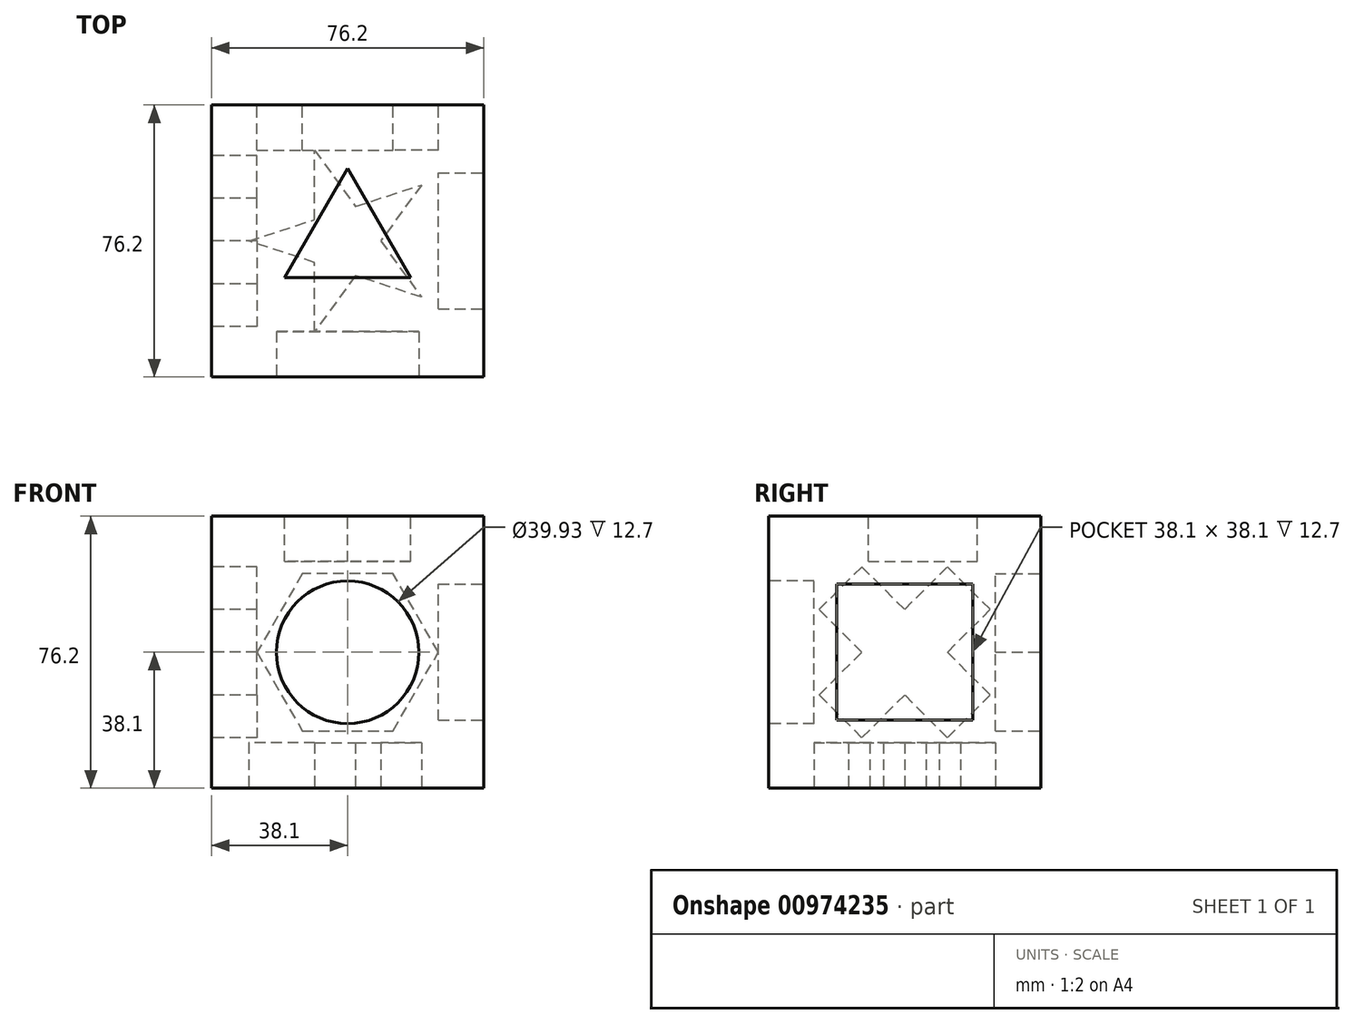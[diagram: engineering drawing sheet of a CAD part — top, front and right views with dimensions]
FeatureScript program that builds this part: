
annotation { "Feature Type Name" : "Feature", "Feature Type Description" : "" }
export const myFeature = defineFeature(function(context is Context, id is Id, definition is map)
    precondition{}
    {
        {
            var Q0;
            Q0=qCreatedBy(makeId("Front.planeOp"),FACE);
            var sketch = newSketch(context, id + "F0", { "sketchPlane" : qUnion([Q0])});
            skLineSegment(sketch, "E0.bottom", {"start": v(-38.1, -38.1) * mm, "end": v(38.1, -38.1) * mm});
            skLineSegment(sketch, "E0.top", {"start": v(-38.1, 38.1) * mm, "end": v(38.1, 38.1) * mm});
            skLineSegment(sketch, "E0.left", {"start": v(-38.1, -38.1) * mm, "end": v(-38.1, 38.1) * mm});
            skLineSegment(sketch, "E0.right", {"start": v(38.1, -38.1) * mm, "end": v(38.1, 38.1) * mm});
            skLineSegment(sketch, "E1", {"start": v(-38.1, 38.1) * mm, "end": v(38.1, -38.1) * mm, "construction": true});
            skSolve(sketch);
        }
        {
            var Q0;
            Q0=makeQuery(id+"F0.imprint","IMPRINT",FACE,{"disambiguationData":[TD([[makeQuery(id+"F0.imprint","IMPRINT",EDGE,{"derivedFrom":sQuery(id+"F0.wireOp",EDGE,"E0.bottom")}),1.0]])]});
            extrude(context, id + "F1", {"entities" : qUnion([Q0]), "depth" : 76.2 * mm, "offsetDistance" : 25.4 * mm});
        }
        {
            var Q0;
            Q0=makeQuery(id+"F1.opExtrude","CAP_FACE",FACE,{"disambiguationData":[OSD([sQuery(id+"F0.wireOp",EDGE,"E0.bottom"),sQuery(id+"F0.wireOp",EDGE,"E0.top"),sQuery(id+"F0.wireOp",EDGE,"E0.left"),sQuery(id+"F0.wireOp",EDGE,"E0.right")])],"isStart":false});
            var sketch = newSketch(context, id + "F2", { "sketchPlane" : qUnion([Q0])});
            skCircle(sketch, "E2", {"center": v(0, 0) * mm, "radius": 19.97 * mm});
            skSolve(sketch);
        }
        {
            var Q0;
            Q0 = qSketchRegion(id + "F2", true);
            var Q1;
            Q1=makeQuery(id+"F2.imprint","IMPRINT",FACE,{"disambiguationData":[TD([[makeQuery(id+"F2.imprint","IMPRINT",EDGE,{"derivedFrom":sQuery(id+"F2.wireOp",EDGE,"E2")}),1.0]])]});
            extrude(context, id + "F3", {"entities" : qUnion([Q0, Q1]), "operationType" : NewBodyOperationType.REMOVE, "oppositeDirection" : true, "depth" : 12.7 * mm, "offsetDistance" : 25.4 * mm});
        }
        {
            var Q0;
            Q0=makeQuery(id+"F1.opExtrude","SWEPT_FACE",FACE,{"disambiguationData":[OSD([sQuery(id+"F0.wireOp",EDGE,"E0.top")])]});
            var sketch = newSketch(context, id + "F4", { "sketchPlane" : qUnion([Q0])});
            skLineSegment(sketch, "E3", {"start": v(-38.1, -38.1) * mm, "end": v(38.1, -38.1) * mm, "construction": true});
            skLineSegment(sketch, "E4", {"start": v(0, -17.72) * mm, "end": v(-17.65, -48.3) * mm});
            skLineSegment(sketch, "E5", {"start": v(-17.65, -48.3) * mm, "end": v(17.65, -48.3) * mm});
            skLineSegment(sketch, "E6", {"start": v(17.65, -48.3) * mm, "end": v(0, -17.72) * mm});
            skPoint(sketch, "E7.orphan", {"position": v(-8.83, -33) * mm});
            skCircle(sketch, "E8", {"center": v(0, -38.1) * mm, "radius": 10.2 * mm, "construction": true});
            skSolve(sketch);
        }
        {
            var Q0;
            Q0=makeQuery(id+"F4.imprint","IMPRINT",FACE,{"disambiguationData":[TD([[makeQuery(id+"F4.imprint","IMPRINT",EDGE,{"derivedFrom":sQuery(id+"F4.wireOp",EDGE,"E4")}),1.0]])]});
            extrude(context, id + "F5", {"entities" : qUnion([Q0]), "operationType" : NewBodyOperationType.REMOVE, "oppositeDirection" : true, "depth" : 12.7 * mm, "offsetDistance" : 25.4 * mm});
        }
        {
            var Q0;
            Q0=makeQuery(id+"F1.opExtrude","SWEPT_FACE",FACE,{"disambiguationData":[OSD([sQuery(id+"F0.wireOp",EDGE,"E0.right")])]});
            var sketch = newSketch(context, id + "F6", { "sketchPlane" : qUnion([Q0])});
            skLineSegment(sketch, "E9.bottom", {"start": v(-57.15, -19.05) * mm, "end": v(-19.05, -19.05) * mm});
            skLineSegment(sketch, "E9.top", {"start": v(-57.15, 19.05) * mm, "end": v(-19.05, 19.05) * mm});
            skLineSegment(sketch, "E9.left", {"start": v(-57.15, -19.05) * mm, "end": v(-57.15, 19.05) * mm});
            skLineSegment(sketch, "E9.right", {"start": v(-19.05, -19.05) * mm, "end": v(-19.05, 19.05) * mm});
            skPoint(sketch, "E9.middle", {"position": v(-38.1, 0) * mm});
            skPoint(sketch, "E9.middle.positionSnap0", {"position": v(-38.1, 38.1) * mm});
            skPoint(sketch, "E9.middle.positionSnap1", {"position": v(-76.2, 0) * mm});
            skPoint(sketch, "E9.centerSnap0", {"position": v(-38.1, 38.1) * mm});
            skPoint(sketch, "E9.centerSnap1", {"position": v(-76.2, 0) * mm});
            skSolve(sketch);
        }
        {
            var Q0;
            Q0=makeQuery(id+"F6.imprint","IMPRINT",FACE,{"disambiguationData":[TD([[makeQuery(id+"F6.imprint","IMPRINT",EDGE,{"derivedFrom":sQuery(id+"F6.wireOp",EDGE,"E9.bottom")}),1.0]])]});
            extrude(context, id + "F7", {"entities" : qUnion([Q0]), "operationType" : NewBodyOperationType.REMOVE, "oppositeDirection" : true, "depth" : 12.7 * mm, "offsetDistance" : 25.4 * mm});
        }
        {
            var Q0;
            Q0=makeQuery(id+"F1.opExtrude","SWEPT_FACE",FACE,{"disambiguationData":[OSD([sQuery(id+"F0.wireOp",EDGE,"E0.left")])]});
            var sketch = newSketch(context, id + "F8", { "sketchPlane" : qUnion([Q0])});
            skLineSegment(sketch, "E10", {"start": v(0, 38.1) * mm, "end": v(76.2, -38.1) * mm, "construction": true});
            skLineSegment(sketch, "E11", {"start": v(0, -38.1) * mm, "end": v(76.2, 38.1) * mm, "construction": true});
            skLineSegment(sketch, "E12", {"start": v(50.07, -23.95) * mm, "end": v(62.05, -11.97) * mm});
            skLineSegment(sketch, "E13", {"start": v(62.05, -11.97) * mm, "end": v(50.07, 0) * mm});
            skLineSegment(sketch, "E14", {"start": v(50.07, 0) * mm, "end": v(62.05, 11.97) * mm});
            skLineSegment(sketch, "E15", {"start": v(62.05, 11.97) * mm, "end": v(50.07, 23.95) * mm});
            skLineSegment(sketch, "E16", {"start": v(50.07, 23.95) * mm, "end": v(38.1, 11.97) * mm});
            skLineSegment(sketch, "E17", {"start": v(38.1, 11.97) * mm, "end": v(26.13, 23.95) * mm});
            skLineSegment(sketch, "E18", {"start": v(26.13, 23.95) * mm, "end": v(14.15, 11.97) * mm});
            skLineSegment(sketch, "E19", {"start": v(14.15, 11.97) * mm, "end": v(26.13, 0) * mm});
            skLineSegment(sketch, "E20", {"start": v(26.13, 0) * mm, "end": v(14.15, -11.97) * mm});
            skLineSegment(sketch, "E21", {"start": v(14.15, -11.97) * mm, "end": v(26.13, -23.95) * mm});
            skLineSegment(sketch, "E22", {"start": v(26.13, -23.95) * mm, "end": v(38.1, -11.97) * mm});
            skLineSegment(sketch, "E23", {"start": v(38.1, -11.97) * mm, "end": v(50.07, -23.95) * mm});
            skSolve(sketch);
        }
        {
            var Q0;
            Q0=makeQuery(id+"F8.imprint","IMPRINT",FACE,{"disambiguationData":[TD([[makeQuery(id+"F8.imprint","IMPRINT",EDGE,{"derivedFrom":sQuery(id+"F8.wireOp",EDGE,"E12")}),1.0]])]});
            extrude(context, id + "F9", {"entities" : qUnion([Q0]), "operationType" : NewBodyOperationType.REMOVE, "oppositeDirection" : true, "depth" : 12.7 * mm, "offsetDistance" : 25.4 * mm});
        }
        {
            var Q0;
            Q0=makeQuery(id+"F1.opExtrude","CAP_FACE",FACE,{"disambiguationData":[OSD([sQuery(id+"F0.wireOp",EDGE,"E0.bottom"),sQuery(id+"F0.wireOp",EDGE,"E0.top"),sQuery(id+"F0.wireOp",EDGE,"E0.left"),sQuery(id+"F0.wireOp",EDGE,"E0.right")])],"isStart":true});
            var sketch = newSketch(context, id + "F10", { "sketchPlane" : qUnion([Q0])});
            skCircle(sketch, "E24.cCircle", {"center": v(0, 0) * mm, "radius": 25.4 * mm, "construction": true});
            skLineSegment(sketch, "E24.0", {"start": v(-25.4, 0) * mm, "end": v(-12.7, 22) * mm});
            skLineSegment(sketch, "E24.1", {"start": v(-12.7, 22) * mm, "end": v(12.7, 22) * mm});
            skLineSegment(sketch, "E24.2", {"start": v(12.7, 22) * mm, "end": v(25.4, 0) * mm});
            skLineSegment(sketch, "E24.3", {"start": v(25.4, 0) * mm, "end": v(12.7, -22) * mm});
            skLineSegment(sketch, "E24.4", {"start": v(12.7, -22) * mm, "end": v(-12.7, -22) * mm});
            skLineSegment(sketch, "E24.5", {"start": v(-12.7, -22) * mm, "end": v(-25.4, 0) * mm});
            skSolve(sketch);
        }
        {
            var Q0;
            Q0=makeQuery(id+"F10.imprint","IMPRINT",FACE,{"disambiguationData":[TD([[makeQuery(id+"F10.imprint","IMPRINT",EDGE,{"derivedFrom":sQuery(id+"F10.wireOp",EDGE,"E24.0")}),-1.0]])]});
            extrude(context, id + "F11", {"entities" : qUnion([Q0]), "operationType" : NewBodyOperationType.REMOVE, "oppositeDirection" : true, "depth" : 12.7 * mm, "offsetDistance" : 25.4 * mm});
        }
        {
            var Q0;
            Q0=makeQuery(id+"F1.opExtrude","SWEPT_FACE",FACE,{"disambiguationData":[OSD([sQuery(id+"F0.wireOp",EDGE,"E0.bottom")])]});
            var sketch = newSketch(context, id + "F12", { "sketchPlane" : qUnion([Q0])});
            skLineSegment(sketch, "E25", {"start": v(20.63, 53.8) * mm, "end": v(-27.68, 38.1) * mm});
            skLineSegment(sketch, "E26", {"start": v(-27.68, 38.1) * mm, "end": v(20.63, 22.4) * mm});
            skLineSegment(sketch, "E27", {"start": v(20.63, 22.4) * mm, "end": v(-9.23, 63.5) * mm});
            skLineSegment(sketch, "E28", {"start": v(-9.23, 63.5) * mm, "end": v(-9.23, 12.7) * mm});
            skLineSegment(sketch, "E29", {"start": v(-9.23, 12.7) * mm, "end": v(20.63, 53.8) * mm});
            skLineSegment(sketch, "E30", {"start": v(0, 76.2) * mm, "end": v(0, 0) * mm, "construction": true});
            skLineSegment(sketch, "E31", {"start": v(38.1, 38.1) * mm, "end": v(0, 38.1) * mm, "construction": true});
            skLineSegment(sketch, "E32", {"start": v(-9.23, 38.1) * mm, "end": v(9.23, 38.1) * mm, "construction": true});
            skSolve(sketch);
        }
        {
            var Q0;
            {var subQ0=sQuery(id+"F12.wireOp",EDGE,"E27");var subQ1=sQuery(id+"F12.wireOp",EDGE,"E25");var subQ2=makeQuery(id+"F12.imprint","INTERSECT",VERTEX,{"derivedFrom":[subQ1,subQ0]});Q0=makeQuery(id+"F12.imprint","IMPRINT",FACE,{"disambiguationData":[TD([[makeQuery(id+"F12.imprint","IMPRINT",EDGE,{"disambiguationData":[TD([[subQ2,-1.0]])],"derivedFrom":subQ1}),-1.0]])]});}
            var Q1;
            {var subQ0=sQuery(id+"F12.wireOp",EDGE,"E26");var subQ1=sQuery(id+"F12.wireOp",EDGE,"E25");var subQ2=makeQuery(id+"F12.imprint","INTERSECT",VERTEX,{"derivedFrom":[subQ1,subQ0]});Q1=makeQuery(id+"F12.imprint","IMPRINT",FACE,{"disambiguationData":[TD([[makeQuery(id+"F12.imprint","IMPRINT",EDGE,{"disambiguationData":[TD([[subQ2,1.0]])],"derivedFrom":subQ1}),1.0]])]});}
            var Q2;
            {var subQ1=sQuery(id+"F12.wireOp",EDGE,"E25");var subQ5=sQuery(id+"F12.wireOp",EDGE,"E27");var subQ6=makeQuery(id+"F12.imprint","INTERSECT",VERTEX,{"derivedFrom":[subQ1,subQ5]});Q2=makeQuery(id+"F12.imprint","IMPRINT",FACE,{"disambiguationData":[TD([[makeQuery(id+"F12.imprint","IMPRINT",EDGE,{"disambiguationData":[TD([[subQ6,-1.0]])],"derivedFrom":subQ1}),1.0]])]});}
            var Q3;
            {var subQ0=sQuery(id+"F12.wireOp",EDGE,"E28");var subQ1=sQuery(id+"F12.wireOp",EDGE,"E26");var subQ2=makeQuery(id+"F12.imprint","INTERSECT",VERTEX,{"derivedFrom":[subQ1,subQ0]});Q3=makeQuery(id+"F12.imprint","IMPRINT",FACE,{"disambiguationData":[TD([[makeQuery(id+"F12.imprint","IMPRINT",EDGE,{"disambiguationData":[TD([[subQ2,-1.0]])],"derivedFrom":subQ1}),-1.0]])]});}
            var Q4;
            {var subQ0=sQuery(id+"F12.wireOp",EDGE,"E27");var subQ1=sQuery(id+"F12.wireOp",EDGE,"E26");var subQ2=makeQuery(id+"F12.imprint","INTERSECT",VERTEX,{"derivedFrom":[subQ1,subQ0]});Q4=makeQuery(id+"F12.imprint","IMPRINT",FACE,{"disambiguationData":[TD([[makeQuery(id+"F12.imprint","IMPRINT",EDGE,{"disambiguationData":[TD([[subQ2,1.0]])],"derivedFrom":subQ1}),1.0]])]});}
            var Q5;
            {var subQ0=sQuery(id+"F12.wireOp",EDGE,"E29");var subQ1=sQuery(id+"F12.wireOp",EDGE,"E25");var subQ2=makeQuery(id+"F12.imprint","INTERSECT",VERTEX,{"derivedFrom":[subQ1,subQ0]});Q5=makeQuery(id+"F12.imprint","IMPRINT",FACE,{"disambiguationData":[TD([[makeQuery(id+"F12.imprint","IMPRINT",EDGE,{"disambiguationData":[TD([[subQ2,-1.0]])],"derivedFrom":subQ1}),1.0]])]});}
            var Q6;
            Q6=sQuery(id+"F12.wireOp",EDGE,"E32");
            extrude(context, id + "F13", {"entities" : qUnion([Q0, Q1, Q2, Q3, Q4, Q5]), "operationType" : NewBodyOperationType.REMOVE, "surfaceEntities" : qUnion([Q6]), "oppositeDirection" : true, "depth" : 12.7 * mm, "offsetDistance" : 25.4 * mm});
        }
    });
